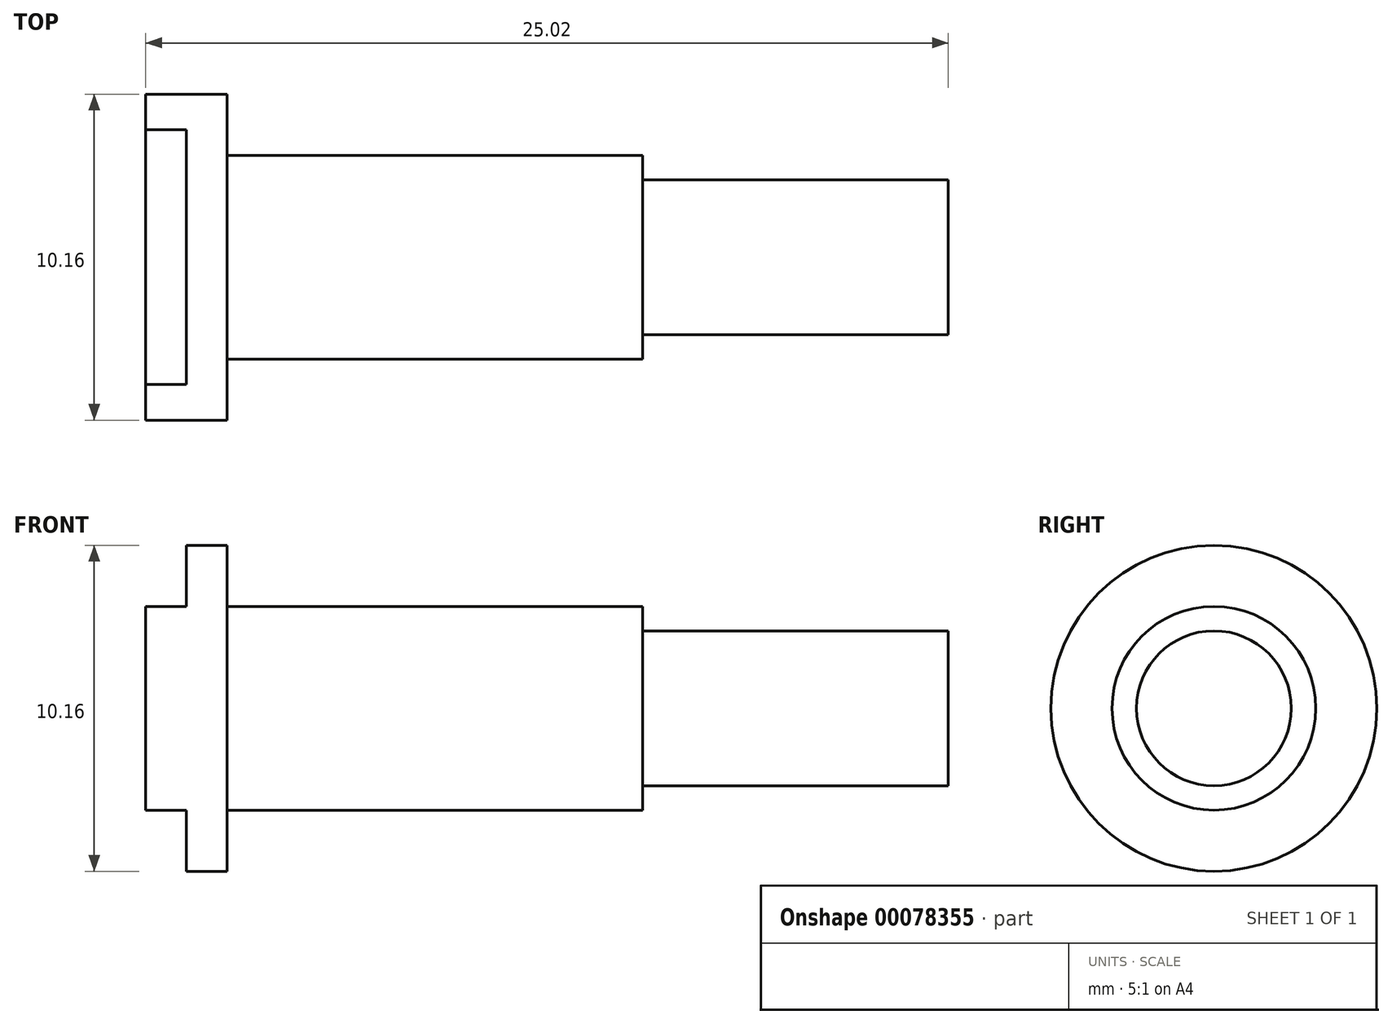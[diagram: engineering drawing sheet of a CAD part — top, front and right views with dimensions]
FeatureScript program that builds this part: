
annotation { "Feature Type Name" : "Feature", "Feature Type Description" : "" }
export const myFeature = defineFeature(function(context is Context, id is Id, definition is map)
    precondition{}
    {
        {
            var Q0;
            Q0=qCreatedBy(makeId("Front.planeOp"),FACE);
            var sketch = newSketch(context, id + "F0", { "sketchPlane" : qUnion([Q0])});
            skLineSegment(sketch, "E0", {"start": v(0, 0) * mm, "end": v(0, 5.08) * mm});
            skLineSegment(sketch, "E1", {"start": v(0, 0) * mm, "end": v(25.02, 0) * mm});
            skLineSegment(sketch, "E2", {"start": v(25.02, 0) * mm, "end": v(25.02, 2.41) * mm});
            skLineSegment(sketch, "E3", {"start": v(0, 5.08) * mm, "end": v(2.54, 5.08) * mm});
            skLineSegment(sketch, "E4", {"start": v(2.54, 3.18) * mm, "end": v(15.5, 3.18) * mm});
            skLineSegment(sketch, "E5", {"start": v(15.5, 3.18) * mm, "end": v(15.5, 2.41) * mm});
            skLineSegment(sketch, "E6", {"start": v(15.5, 2.41) * mm, "end": v(25.02, 2.41) * mm});
            skLineSegment(sketch, "E7", {"start": v(2.54, 5.08) * mm, "end": v(2.54, 3.18) * mm});
            skSolve(sketch);
        }
        {
            var Q0;
            Q0 = qSketchRegion(id + "F0", true);
            var Q1;
            Q1=sQuery(id+"F0.wireOp",EDGE,"E1");
            revolve(context, id + "F1", {"entities" : qUnion([Q0]), "axis" : qUnion([Q1]), "revolveType" : RevolveType.FULL});
        }
        {
            var Q0;
            Q0=qCreatedBy(makeId("Right.planeOp"),FACE);
            cPlane(context, id + "F2", {"entities" : qUnion([Q0]), "cplaneType" : CPlaneType.OFFSET, "offset" : 2.54 * mm, "oppositeDirection" : true, "width" : 152.4 * mm, "height" : 152.4 * mm});
        }
        {
            var Q0;
            Q0=qCreatedBy(id+"F2.planeOp",FACE);
            var sketch = newSketch(context, id + "F3", { "sketchPlane" : qUnion([Q0])});
            skLineSegment(sketch, "E8", {"start": v(0, 0) * mm, "end": v(0, 3.18) * mm, "construction": true});
            skLineSegment(sketch, "E9", {"start": v(0, 3.18) * mm, "end": v(5.87, 3.18) * mm});
            skLineSegment(sketch, "E10.MirrorCS", {"start": v(0, 3.18) * mm, "end": v(-5.87, 3.18) * mm});
            skLineSegment(sketch, "E11.MirrorCS", {"start": v(0, -3.18) * mm, "end": v(5.87, -3.18) * mm});
            skLineSegment(sketch, "E12.MirrorCS", {"start": v(0, -3.18) * mm, "end": v(-5.87, -3.18) * mm});
            skLineSegment(sketch, "E13", {"start": v(-5.87, 3.18) * mm, "end": v(-5.87, 6.3) * mm});
            skLineSegment(sketch, "E14", {"start": v(-5.87, 6.3) * mm, "end": v(5.87, 6.3) * mm});
            skLineSegment(sketch, "E15", {"start": v(5.87, 6.3) * mm, "end": v(5.87, 3.18) * mm});
            skLineSegment(sketch, "E16.MirrorCS", {"start": v(5.87, -6.3) * mm, "end": v(5.87, -3.18) * mm});
            skLineSegment(sketch, "E17.MirrorCS", {"start": v(-5.87, -6.3) * mm, "end": v(5.87, -6.3) * mm});
            skLineSegment(sketch, "E18.MirrorCS", {"start": v(-5.87, -3.18) * mm, "end": v(-5.87, -6.3) * mm});
            skSolve(sketch);
        }
        {
            var Q0;
            Q0 = qSketchRegion(id + "F3", true);
            extrude(context, id + "F4", {"entities" : qUnion([Q0]), "operationType" : NewBodyOperationType.REMOVE, "depth" : 3.81 * mm});
        }
    });
